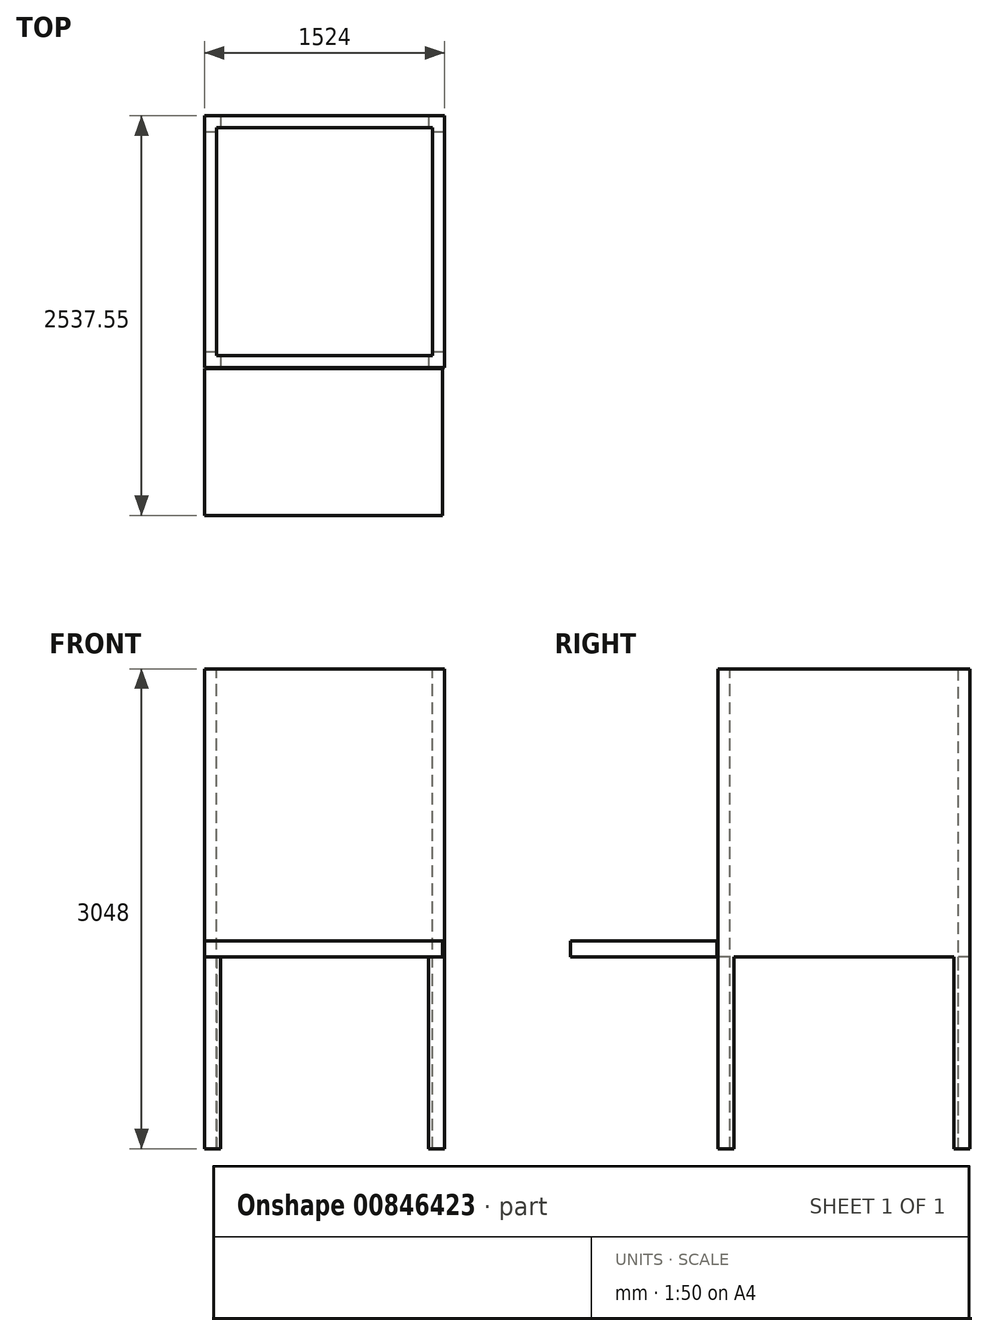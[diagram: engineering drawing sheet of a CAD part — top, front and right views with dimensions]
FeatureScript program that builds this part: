
annotation { "Feature Type Name" : "Feature", "Feature Type Description" : "" }
export const myFeature = defineFeature(function(context is Context, id is Id, definition is map)
    precondition{}
    {
        {
            var Q0;
            Q0=qCreatedBy(makeId("Front.planeOp"),FACE);
            var sketch = newSketch(context, id + "F0", { "sketchPlane" : qUnion([Q0])});
            skLineSegment(sketch, "E0.bottom", {"start": v(0, 0) * mm, "end": v(1524, 0) * mm});
            skLineSegment(sketch, "E0.top", {"start": v(0, 3048) * mm, "end": v(1524, 3048) * mm});
            skLineSegment(sketch, "E0.left", {"start": v(0, 0) * mm, "end": v(0, 3048) * mm});
            skLineSegment(sketch, "E0.right", {"start": v(1524, 0) * mm, "end": v(1524, 3048) * mm});
            skSolve(sketch);
        }
        {
            var Q0;
            Q0=makeQuery(id+"F0.imprint","IMPRINT",FACE,{"disambiguationData":[TD([[makeQuery(id+"F0.imprint","IMPRINT",EDGE,{"derivedFrom":sQuery(id+"F0.wireOp",EDGE,"E0.bottom")}),1.0]])]});
            extrude(context, id + "F1", {"entities" : qUnion([Q0]), "depth" : 76.2 * mm, "offsetDistance" : 25.4 * mm});
        }
        {
            var Q0;
            Q0=makeQuery(id+"F1.opExtrude","SWEPT_FACE",FACE,{"disambiguationData":[OSD([sQuery(id+"F0.wireOp",EDGE,"E0.right")])]});
            var sketch = newSketch(context, id + "F2", { "sketchPlane" : qUnion([Q0])});
            skLineSegment(sketch, "E1.bottom", {"start": v(0, 3048) * mm, "end": v(1524, 3048) * mm});
            skLineSegment(sketch, "E1.top", {"start": v(0, 0) * mm, "end": v(1524, 0) * mm});
            skLineSegment(sketch, "E1.left", {"start": v(0, 3048) * mm, "end": v(0, 0) * mm});
            skLineSegment(sketch, "E1.right", {"start": v(1524, 3048) * mm, "end": v(1524, 0) * mm});
            skSolve(sketch);
        }
        {
            var Q0;
            Q0=makeQuery(id+"F2.imprint","IMPRINT",FACE,{"disambiguationData":[TD([[makeQuery(id+"F2.imprint","IMPRINT",EDGE,{"derivedFrom":sQuery(id+"F2.wireOp",EDGE,"E1.bottom")}),-1.0]])]});
            extrude(context, id + "F3", {"entities" : qUnion([Q0]), "operationType" : NewBodyOperationType.ADD, "oppositeDirection" : true, "depth" : 76.2 * mm, "offsetDistance" : 25.4 * mm});
        }
        {
            var Q0;
            Q0=makeQuery(id+"F1.opExtrude","SWEPT_FACE",FACE,{"disambiguationData":[OSD([sQuery(id+"F0.wireOp",EDGE,"E0.left")])]});
            var sketch = newSketch(context, id + "F4", { "sketchPlane" : qUnion([Q0])});
            skLineSegment(sketch, "E2.bottom", {"start": v(0, 3048) * mm, "end": v(-1524, 3048) * mm});
            skLineSegment(sketch, "E2.top", {"start": v(0, 0) * mm, "end": v(-1524, 0) * mm});
            skLineSegment(sketch, "E2.left", {"start": v(0, 3048) * mm, "end": v(0, 0) * mm});
            skLineSegment(sketch, "E2.right", {"start": v(-1524, 3048) * mm, "end": v(-1524, 0) * mm});
            skSolve(sketch);
        }
        {
            var Q0;
            Q0 = qSketchRegion(id + "F4", true);
            extrude(context, id + "F5", {"entities" : qUnion([Q0]), "operationType" : NewBodyOperationType.ADD, "oppositeDirection" : true, "depth" : 76.2 * mm, "offsetDistance" : 25.4 * mm});
        }
        {
            var Q0;
            Q0=makeQuery(id+"F3.opExtrude","SWEPT_FACE",FACE,{"disambiguationData":[OSD([sQuery(id+"F2.wireOp",EDGE,"E1.right")])]});
            var sketch = newSketch(context, id + "F6", { "sketchPlane" : qUnion([Q0])});
            skLineSegment(sketch, "E3.bottom", {"start": v(-1447.8, 3048) * mm, "end": v(-76.2, 3048) * mm});
            skLineSegment(sketch, "E3.top", {"start": v(-1447.8, 0) * mm, "end": v(-76.2, 0) * mm});
            skLineSegment(sketch, "E3.left", {"start": v(-1447.8, 3048) * mm, "end": v(-1447.8, 0) * mm});
            skLineSegment(sketch, "E3.right", {"start": v(-76.2, 3048) * mm, "end": v(-76.2, 0) * mm});
            skSolve(sketch);
        }
        {
            var Q0;
            Q0 = qSketchRegion(id + "F6", true);
            extrude(context, id + "F7", {"entities" : qUnion([Q0]), "operationType" : NewBodyOperationType.ADD, "oppositeDirection" : true, "depth" : 76.2 * mm, "offsetDistance" : 25.4 * mm});
        }
        {
            var Q0;
            Q0=makeQuery(id+"F3.boolean.opBoolean","MERGE",FACE,{"derivedFrom":[makeQuery(id+"F1.opExtrude","SWEPT_FACE",FACE,{"disambiguationData":[OSD([sQuery(id+"F0.wireOp",EDGE,"E0.right")])]}),makeQuery(id+"F3.opExtrude","CAP_FACE",FACE,{"disambiguationData":[OSD([sQuery(id+"F2.wireOp",EDGE,"E1.bottom"),sQuery(id+"F2.wireOp",EDGE,"E1.top"),sQuery(id+"F2.wireOp",EDGE,"E1.left"),sQuery(id+"F2.wireOp",EDGE,"E1.right")])],"isStart":true})]});
            var sketch = newSketch(context, id + "F8", { "sketchPlane" : qUnion([Q0])});
            skLineSegment(sketch, "E4.bottom", {"start": v(25.4, 0) * mm, "end": v(1422.4, 0) * mm});
            skLineSegment(sketch, "E4.top", {"start": v(25.4, 1219.2) * mm, "end": v(1422.4, 1219.2) * mm});
            skLineSegment(sketch, "E4.left", {"start": v(25.4, 0) * mm, "end": v(25.4, 1219.2) * mm});
            skLineSegment(sketch, "E4.right", {"start": v(1422.4, 0) * mm, "end": v(1422.4, 1219.2) * mm});
            skSolve(sketch);
        }
        {
            var Q0;
            Q0=makeQuery(id+"F8.imprint","IMPRINT",FACE,{"disambiguationData":[TD([[makeQuery(id+"F8.imprint","IMPRINT",EDGE,{"derivedFrom":sQuery(id+"F8.wireOp",EDGE,"E4.bottom")}),1.0]])]});
            extrude(context, id + "F9", {"entities" : qUnion([Q0]), "operationType" : NewBodyOperationType.REMOVE, "oppositeDirection" : true, "depth" : 1574.8 * mm, "offsetDistance" : 25.4 * mm});
        }
        {
            var Q0;
            Q0=makeQuery(id+"F1.opExtrude","CAP_FACE",FACE,{"disambiguationData":[OSD([sQuery(id+"F0.wireOp",EDGE,"E0.bottom"),sQuery(id+"F0.wireOp",EDGE,"E0.top"),sQuery(id+"F0.wireOp",EDGE,"E0.left"),sQuery(id+"F0.wireOp",EDGE,"E0.right")])],"isStart":false});
            var sketch = newSketch(context, id + "F10", { "sketchPlane" : qUnion([Q0])});
            skLineSegment(sketch, "E5.bottom", {"start": v(101.6, 0) * mm, "end": v(1422.4, 0) * mm});
            skLineSegment(sketch, "E5.top", {"start": v(101.6, 1219.2) * mm, "end": v(1422.4, 1219.2) * mm});
            skLineSegment(sketch, "E5.left", {"start": v(101.6, 0) * mm, "end": v(101.6, 1219.2) * mm});
            skLineSegment(sketch, "E5.right", {"start": v(1422.4, 0) * mm, "end": v(1422.4, 1219.2) * mm});
            skSolve(sketch);
        }
        {
            var Q0;
            Q0 = qSketchRegion(id + "F10", true);
            extrude(context, id + "F11", {"entities" : qUnion([Q0]), "operationType" : NewBodyOperationType.REMOVE, "oppositeDirection" : true, "depth" : 1676.4 * mm, "offsetDistance" : 25.4 * mm});
        }
        {
            var Q0;
            {var subQ0=sQuery(id+"F0.wireOp",EDGE,"E0.right");var subQ1=sQuery(id+"F0.wireOp",EDGE,"E0.left");var subQ2=sQuery(id+"F0.wireOp",EDGE,"E0.top");var subQ3=sQuery(id+"F0.wireOp",EDGE,"E0.bottom");Q0=makeQuery(id+"F11.boolean.opBoolean","COPY",FACE,{"disambiguationData":[TD([makeQuery(id+"F1.opExtrude","CAP_FACE",FACE,{"disambiguationData":[OSD([subQ3,subQ2,subQ1,subQ0])],"isStart":true})])],"derivedFrom":makeQuery(id+"F11.opExtrude","SWEPT_FACE",FACE,{"disambiguationData":[OSD([sQuery(id+"F10.wireOp",EDGE,"E5.top")])]})});}
            var sketch = newSketch(context, id + "F12", { "sketchPlane" : qUnion([Q0])});
            skLineSegment(sketch, "E6.bottom", {"start": v(1511.7, 82.32) * mm, "end": v(0, 82.32) * mm});
            skLineSegment(sketch, "E6.top", {"start": v(1511.7, 1013.55) * mm, "end": v(0, 1013.55) * mm});
            skLineSegment(sketch, "E6.left", {"start": v(1511.7, 82.32) * mm, "end": v(1511.7, 1013.55) * mm});
            skLineSegment(sketch, "E6.right", {"start": v(0, 82.32) * mm, "end": v(0, 1013.55) * mm});
            skSolve(sketch);
        }
        {
            var Q0;
            Q0=makeQuery(id+"F12.imprint","IMPRINT",FACE,{"disambiguationData":[TD([[makeQuery(id+"F12.imprint","IMPRINT",EDGE,{"derivedFrom":sQuery(id+"F12.wireOp",EDGE,"E6.bottom")}),-1.0]])]});
            extrude(context, id + "F13", {"entities" : qUnion([Q0]), "oppositeDirection" : true, "depth" : 101.6 * mm, "offsetDistance" : 25.4 * mm});
        }
    });
